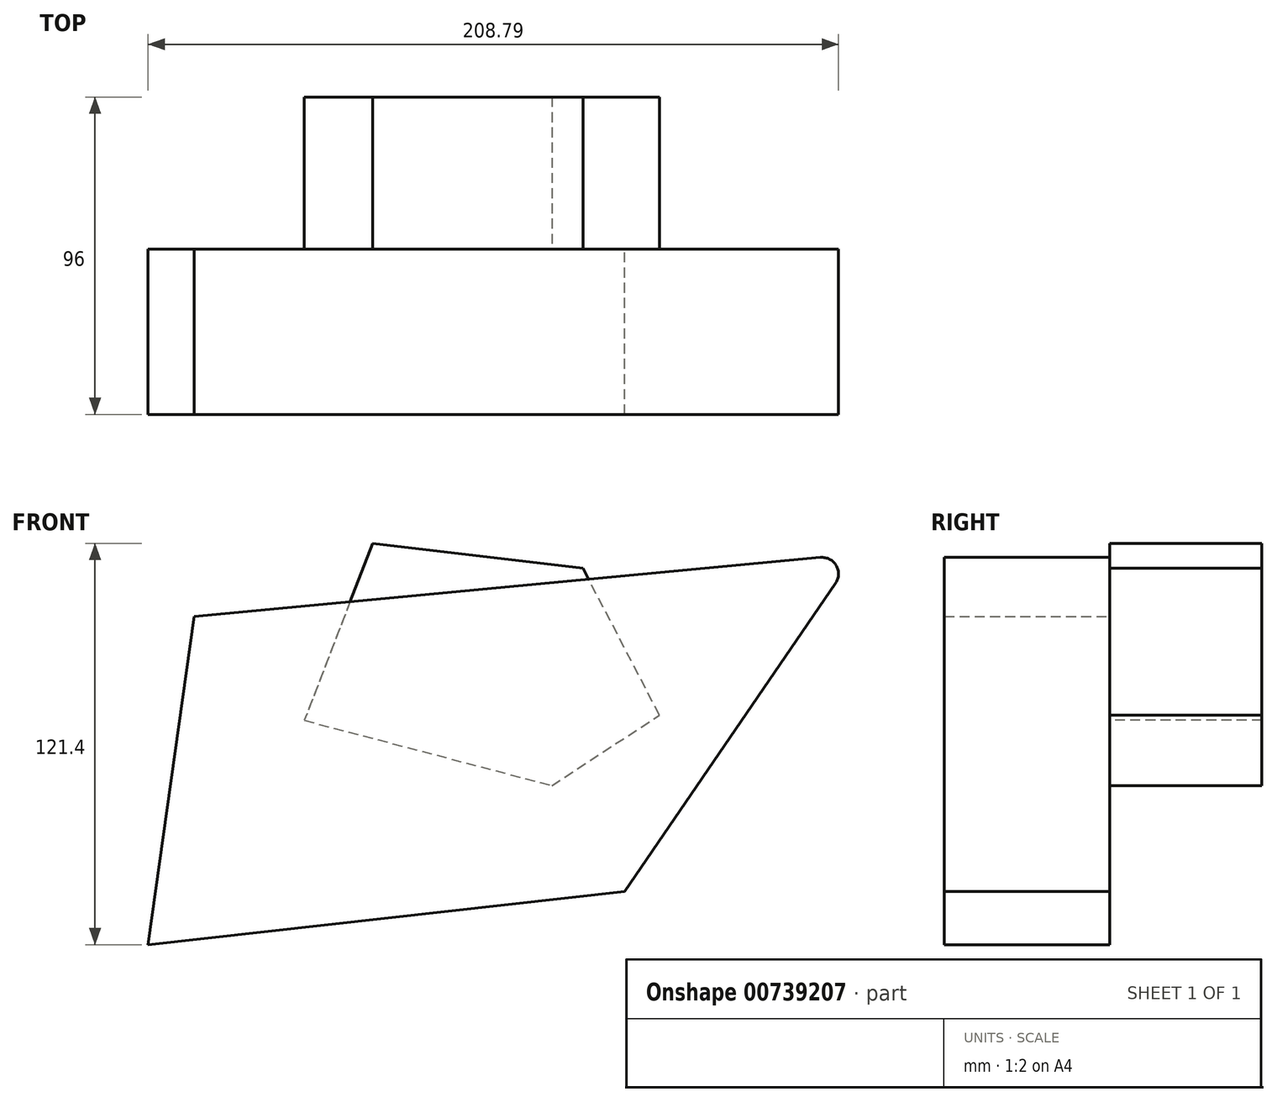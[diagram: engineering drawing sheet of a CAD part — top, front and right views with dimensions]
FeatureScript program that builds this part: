
annotation { "Feature Type Name" : "Feature", "Feature Type Description" : "" }
export const myFeature = defineFeature(function(context is Context, id is Id, definition is map)
    precondition{}
    {
        {
            var Q0;
            Q0=qCreatedBy(makeId("Front.planeOp"),FACE);
            var sketch = newSketch(context, id + "F0", { "sketchPlane" : qUnion([Q0])});
            skLineSegment(sketch, "E0", {"start": v(-62.95, 36.89) * mm, "end": v(-46.8, -22.3) * mm});
            skLineSegment(sketch, "E1", {"start": v(-46.8, -22.3) * mm, "end": v(34.61, -16.01) * mm});
            skLineSegment(sketch, "E2", {"start": v(34.61, -16.01) * mm, "end": v(26.36, 40.07) * mm});
            skLineSegment(sketch, "E3", {"start": v(26.36, 40.07) * mm, "end": v(-62.95, 36.89) * mm});
            skSolve(sketch);
        }
        {
            var Q0;
            Q0=makeQuery(id+"F0.imprint","IMPRINT",FACE,{"disambiguationData":[TD([[makeQuery(id+"F0.imprint","IMPRINT",EDGE,{"derivedFrom":sQuery(id+"F0.wireOp",EDGE,"E0")}),1.0]])]});
            extrude(context, id + "F1", {"entities" : qUnion([Q0]), "depth" : 30 * mm, "offsetDistance" : 25.4 * mm});
        }
        {
            var Q0;
            Q0=makeQuery(id+"F1.opExtrude","SWEPT_BODY",BODY,{"disambiguationData":[OSD([sQuery(id+"F0.wireOp",EDGE,"E0"),sQuery(id+"F0.wireOp",EDGE,"E1"),sQuery(id+"F0.wireOp",EDGE,"E2"),sQuery(id+"F0.wireOp",EDGE,"E3")])]});
            deleteBodies(context, id + "F2", {"entities" : qUnion([Q0])});
        }
        {
            var Q0;
            Q0=qCreatedBy(makeId("Front.planeOp"),FACE);
            var sketch = newSketch(context, id + "F3", { "sketchPlane" : qUnion([Q0])});
            skLineSegment(sketch, "E4", {"start": v(-98.64, 34.25) * mm, "end": v(101.36, 53.08) * mm});
            skLineSegment(sketch, "E5", {"start": v(101.36, 53.08) * mm, "end": v(31.47, -49.01) * mm});
            skLineSegment(sketch, "E6", {"start": v(31.47, -49.01) * mm, "end": v(-112.58, -65.04) * mm});
            skLineSegment(sketch, "E7", {"start": v(-112.58, -65.04) * mm, "end": v(-98.64, 34.25) * mm});
            skSolve(sketch);
        }
        {
            var Q0;
            Q0=makeQuery(id+"F3.imprint","IMPRINT",FACE,{"disambiguationData":[TD([[makeQuery(id+"F3.imprint","IMPRINT",EDGE,{"derivedFrom":sQuery(id+"F3.wireOp",EDGE,"E4")}),-1.0]])]});
            extrude(context, id + "F4", {"entities" : qUnion([Q0]), "depth" : 50 * mm, "offsetDistance" : 25 * mm});
        }
        {
            var Q0;
            Q0=makeQuery(id+"F4.opExtrude","SWEPT_EDGE",EDGE,{"disambiguationData":[OSD([sQuery(id+"F3.wireOp",EDGE,"E4"),sQuery(id+"F3.wireOp",EDGE,"E5")])]});
            fillet(context, id + "F5", {"entities" : qUnion([Q0]), "radius" : 5 * mm, "tangentPropagation" : true, "allowEdgeOverflow" : false});
        }
        {
            var Q0;
            Q0=qCreatedBy(makeId("Front.planeOp"),FACE);
            var sketch = newSketch(context, id + "F6", { "sketchPlane" : qUnion([Q0])});
            skLineSegment(sketch, "E8", {"start": v(-44.67, 56.36) * mm, "end": v(-65.33, 2.82) * mm});
            skLineSegment(sketch, "E9", {"start": v(-65.33, 2.82) * mm, "end": v(9.5, -16.9) * mm});
            skLineSegment(sketch, "E10", {"start": v(9.5, -16.9) * mm, "end": v(42.07, 4.38) * mm});
            skLineSegment(sketch, "E11", {"start": v(42.07, 4.38) * mm, "end": v(18.9, 48.85) * mm});
            skLineSegment(sketch, "E12", {"start": v(18.9, 48.85) * mm, "end": v(-44.67, 56.36) * mm});
            skSolve(sketch);
        }
        {
            var Q0;
            Q0=makeQuery(id+"F6.imprint","IMPRINT",FACE,{"disambiguationData":[TD([[makeQuery(id+"F6.imprint","IMPRINT",EDGE,{"derivedFrom":sQuery(id+"F6.wireOp",EDGE,"E8")}),1.0]])]});
            extrude(context, id + "F7", {"entities" : qUnion([Q0]), "operationType" : NewBodyOperationType.ADD, "oppositeDirection" : true, "depth" : 46 * mm, "offsetDistance" : 25 * mm});
        }
    });
